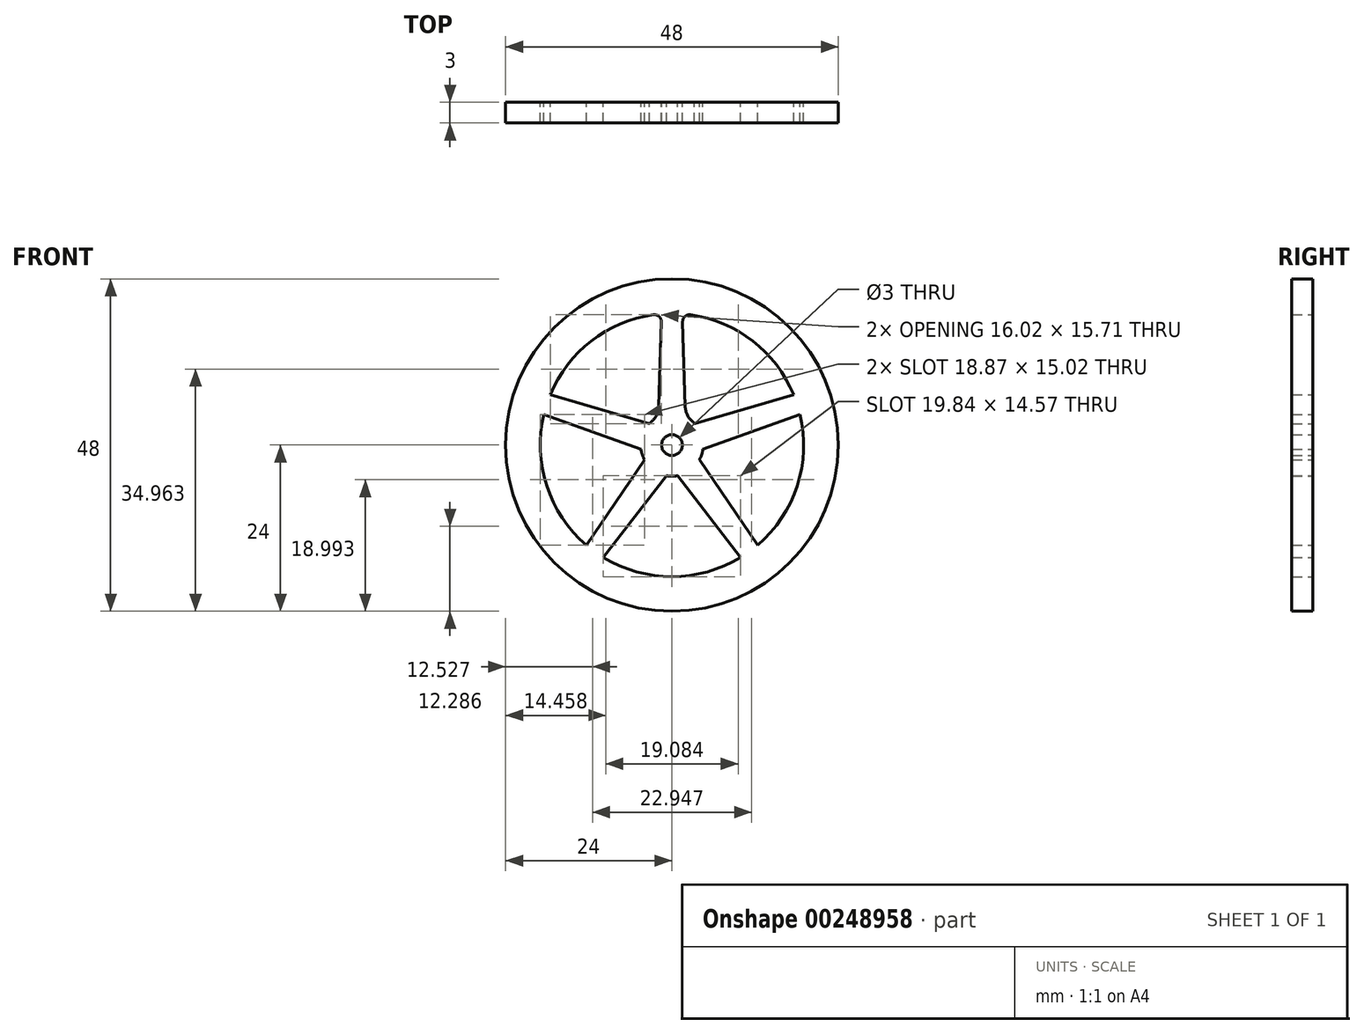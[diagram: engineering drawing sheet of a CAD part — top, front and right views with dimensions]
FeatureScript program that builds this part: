
annotation { "Feature Type Name" : "Feature", "Feature Type Description" : "" }
export const myFeature = defineFeature(function(context is Context, id is Id, definition is map)
    precondition{}
    {
        {
            var Q0;
            Q0=qCreatedBy(makeId("Front.planeOp"),FACE);
            var sketch = newSketch(context, id + "F0", { "sketchPlane" : qUnion([Q0])});
            skCircle(sketch, "E0", {"center": v(0, 0) * mm, "radius": 24 * mm});
            skCircle(sketch, "E1", {"center": v(0, 0) * mm, "radius": 1.5 * mm});
            skCircle(sketch, "E2", {"center": v(0, 0) * mm, "radius": 4.5 * mm});
            skCircle(sketch, "E3", {"center": v(0, 0) * mm, "radius": 19 * mm});
            skLineSegment(sketch, "E4", {"start": v(0, 0) * mm, "end": v(0, 1.5) * mm, "construction": true});
            skLineSegment(sketch, "E5", {"start": v(-1.95, 4.06) * mm, "end": v(-1.5, 18.94) * mm});
            skPoint(sketch, "E6.MirrorCS.end.orphan", {"position": v(1.5, 18.94) * mm});
            skPoint(sketch, "E6.MirrorCS.start.orphan", {"position": v(1.95, 4.06) * mm});
            skLineSegment(sketch, "E7.MirrorCS", {"start": v(1.95, 4.06) * mm, "end": v(1.5, 18.94) * mm});
            skSolve(sketch);
        }
        {
            var Q0;
            Q0=makeQuery(id+"F0.imprint","IMPRINT",FACE,{"disambiguationData":[TD([[makeQuery(id+"F0.imprint","IMPRINT",EDGE,{"derivedFrom":sQuery(id+"F0.wireOp",EDGE,"E0")}),1.0]])]});
            var Q1;
            Q1=makeQuery(id+"F0.imprint","IMPRINT",FACE,{"disambiguationData":[TD([[makeQuery(id+"F0.imprint","IMPRINT",EDGE,{"derivedFrom":sQuery(id+"F0.wireOp",EDGE,"E1")}),-1.0]])]});
            var Q2;
            {var subQ0=sQuery(id+"F0.wireOp",EDGE,"E5");Q2=makeQuery(id+"F0.imprint","IMPRINT",FACE,{"disambiguationData":[TD([[makeQuery(id+"F0.imprint","IMPRINT",EDGE,{"derivedFrom":subQ0}),-1.0]])]});}
            var Q3;
            Q3=sQuery(id+"F0.wireOp",EDGE,"E1");
            var Q4;
            Q4=sQuery(id+"F0.wireOp",EDGE,"E0");
            extrude(context, id + "F1", {"entities" : qUnion([Q0, Q1, Q2]), "surfaceEntities" : qUnion([Q3, Q4]), "depth" : 3 * mm});
        }
        {
            var Q0;
            Q0=makeQuery(id+"F1.opExtrude","SWEPT_BODY",BODY,{"disambiguationData":[OSD([sQuery(id+"F0.wireOp",EDGE,"E0"),sQuery(id+"F0.wireOp",EDGE,"E1"),sQuery(id+"F0.wireOp",EDGE,"E2"),sQuery(id+"F0.wireOp",EDGE,"E3"),sQuery(id+"F0.wireOp",EDGE,"E5"),sQuery(id+"F0.wireOp",EDGE,"E7.MirrorCS")])]});
            var Q1;
            Q1=makeQuery(id+"F1.opExtrude","SWEPT_FACE",FACE,{"disambiguationData":[OSD([sQuery(id+"F0.wireOp",EDGE,"E0")])]});
            circularPattern(context, id + "F2", {"operationType" : NewBodyOperationType.ADD, "entities" : qUnion([Q0]), "axis" : qUnion([Q1]), "angle" : 360 * degree, "instanceCount" : 5, "equalSpace" : true});
        }
        {
            var Q0;
            Q0=makeQuery(id+"F1.opExtrude","SWEPT_EDGE",EDGE,{"disambiguationData":[OSD([sQuery(id+"F0.wireOp",EDGE,"E2"),sQuery(id+"F0.wireOp",EDGE,"E5")])]});
            var Q1;
            Q1=makeQuery(id+"F2.opPattern","COPY",EDGE,{"derivedFrom":makeQuery(id+"F1.opExtrude","SWEPT_EDGE",EDGE,{"disambiguationData":[OSD([sQuery(id+"F0.wireOp",EDGE,"E2"),sQuery(id+"F0.wireOp",EDGE,"E7.MirrorCS")])]}),"instanceName":"4"});
            var Q2;
            Q2=makeQuery(id+"F2.opPattern","COPY",EDGE,{"derivedFrom":makeQuery(id+"F1.opExtrude","SWEPT_EDGE",EDGE,{"disambiguationData":[OSD([sQuery(id+"F0.wireOp",EDGE,"E2"),sQuery(id+"F0.wireOp",EDGE,"E5")])]}),"instanceName":"1"});
            var Q3;
            Q3=makeQuery(id+"F1.opExtrude","SWEPT_EDGE",EDGE,{"disambiguationData":[OSD([sQuery(id+"F0.wireOp",EDGE,"E2"),sQuery(id+"F0.wireOp",EDGE,"E7.MirrorCS")])]});
            var Q4;
            Q4=makeQuery(id+"F2.opPattern","COPY",EDGE,{"derivedFrom":makeQuery(id+"F1.opExtrude","SWEPT_EDGE",EDGE,{"disambiguationData":[OSD([sQuery(id+"F0.wireOp",EDGE,"E2"),sQuery(id+"F0.wireOp",EDGE,"E5")])]}),"instanceName":"2"});
            var Q5;
            Q5=makeQuery(id+"F2.opPattern","COPY",EDGE,{"derivedFrom":makeQuery(id+"F1.opExtrude","SWEPT_EDGE",EDGE,{"disambiguationData":[OSD([sQuery(id+"F0.wireOp",EDGE,"E2"),sQuery(id+"F0.wireOp",EDGE,"E7.MirrorCS")])]}),"instanceName":"1"});
            var Q6;
            Q6=makeQuery(id+"F2.opPattern","COPY",EDGE,{"derivedFrom":makeQuery(id+"F1.opExtrude","SWEPT_EDGE",EDGE,{"disambiguationData":[OSD([sQuery(id+"F0.wireOp",EDGE,"E2"),sQuery(id+"F0.wireOp",EDGE,"E7.MirrorCS")])]}),"instanceName":"2"});
            var Q7;
            Q7=makeQuery(id+"F2.opPattern","COPY",EDGE,{"derivedFrom":makeQuery(id+"F1.opExtrude","SWEPT_EDGE",EDGE,{"disambiguationData":[OSD([sQuery(id+"F0.wireOp",EDGE,"E2"),sQuery(id+"F0.wireOp",EDGE,"E5")])]}),"instanceName":"3"});
            var Q8;
            Q8=makeQuery(id+"F2.opPattern","COPY",EDGE,{"derivedFrom":makeQuery(id+"F1.opExtrude","SWEPT_EDGE",EDGE,{"disambiguationData":[OSD([sQuery(id+"F0.wireOp",EDGE,"E2"),sQuery(id+"F0.wireOp",EDGE,"E7.MirrorCS")])]}),"instanceName":"3"});
            var Q9;
            Q9=makeQuery(id+"F2.opPattern","COPY",EDGE,{"derivedFrom":makeQuery(id+"F1.opExtrude","SWEPT_EDGE",EDGE,{"disambiguationData":[OSD([sQuery(id+"F0.wireOp",EDGE,"E2"),sQuery(id+"F0.wireOp",EDGE,"E5")])]}),"instanceName":"4"});
            fillet(context, id + "F3", {"entities" : qUnion([Q0, Q1, Q2, Q3, Q4, Q5, Q6, Q7, Q8, Q9]), "radius" : 3 * mm, "tangentPropagation" : true, "allowEdgeOverflow" : false});
        }
        {
            var Q0;
            Q0=makeQuery(id+"F1.opExtrude","SWEPT_EDGE",EDGE,{"disambiguationData":[OSD([sQuery(id+"F0.wireOp",EDGE,"E3"),sQuery(id+"F0.wireOp",EDGE,"E5")])]});
            var Q1;
            Q1=makeQuery(id+"F2.opPattern","COPY",EDGE,{"derivedFrom":makeQuery(id+"F1.opExtrude","SWEPT_EDGE",EDGE,{"disambiguationData":[OSD([sQuery(id+"F0.wireOp",EDGE,"E3"),sQuery(id+"F0.wireOp",EDGE,"E5")])]}),"instanceName":"1"});
            var Q2;
            Q2=makeQuery(id+"F2.opPattern","COPY",EDGE,{"derivedFrom":makeQuery(id+"F1.opExtrude","SWEPT_EDGE",EDGE,{"disambiguationData":[OSD([sQuery(id+"F0.wireOp",EDGE,"E3"),sQuery(id+"F0.wireOp",EDGE,"E7.MirrorCS")])]}),"instanceName":"2"});
            var Q3;
            Q3=makeQuery(id+"F2.opPattern","COPY",EDGE,{"derivedFrom":makeQuery(id+"F1.opExtrude","SWEPT_EDGE",EDGE,{"disambiguationData":[OSD([sQuery(id+"F0.wireOp",EDGE,"E3"),sQuery(id+"F0.wireOp",EDGE,"E7.MirrorCS")])]}),"instanceName":"1"});
            var Q4;
            Q4=makeQuery(id+"F1.opExtrude","SWEPT_EDGE",EDGE,{"disambiguationData":[OSD([sQuery(id+"F0.wireOp",EDGE,"E3"),sQuery(id+"F0.wireOp",EDGE,"E7.MirrorCS")])]});
            var Q5;
            Q5=makeQuery(id+"F2.opPattern","COPY",EDGE,{"derivedFrom":makeQuery(id+"F1.opExtrude","SWEPT_EDGE",EDGE,{"disambiguationData":[OSD([sQuery(id+"F0.wireOp",EDGE,"E3"),sQuery(id+"F0.wireOp",EDGE,"E5")])]}),"instanceName":"4"});
            var Q6;
            Q6=makeQuery(id+"F2.opPattern","COPY",EDGE,{"derivedFrom":makeQuery(id+"F1.opExtrude","SWEPT_EDGE",EDGE,{"disambiguationData":[OSD([sQuery(id+"F0.wireOp",EDGE,"E3"),sQuery(id+"F0.wireOp",EDGE,"E7.MirrorCS")])]}),"instanceName":"3"});
            var Q7;
            Q7=makeQuery(id+"F2.opPattern","COPY",EDGE,{"derivedFrom":makeQuery(id+"F1.opExtrude","SWEPT_EDGE",EDGE,{"disambiguationData":[OSD([sQuery(id+"F0.wireOp",EDGE,"E3"),sQuery(id+"F0.wireOp",EDGE,"E5")])]}),"instanceName":"2"});
            var Q8;
            Q8=makeQuery(id+"F2.opPattern","COPY",EDGE,{"derivedFrom":makeQuery(id+"F1.opExtrude","SWEPT_EDGE",EDGE,{"disambiguationData":[OSD([sQuery(id+"F0.wireOp",EDGE,"E3"),sQuery(id+"F0.wireOp",EDGE,"E5")])]}),"instanceName":"3"});
            var Q9;
            Q9=makeQuery(id+"F2.opPattern","COPY",EDGE,{"derivedFrom":makeQuery(id+"F1.opExtrude","SWEPT_EDGE",EDGE,{"disambiguationData":[OSD([sQuery(id+"F0.wireOp",EDGE,"E3"),sQuery(id+"F0.wireOp",EDGE,"E7.MirrorCS")])]}),"instanceName":"4"});
            fillet(context, id + "F4", {"entities" : qUnion([Q0, Q1, Q2, Q3, Q4, Q5, Q6, Q7, Q8, Q9]), "radius" : 1 * mm, "tangentPropagation" : true, "allowEdgeOverflow" : false});
        }
    });
